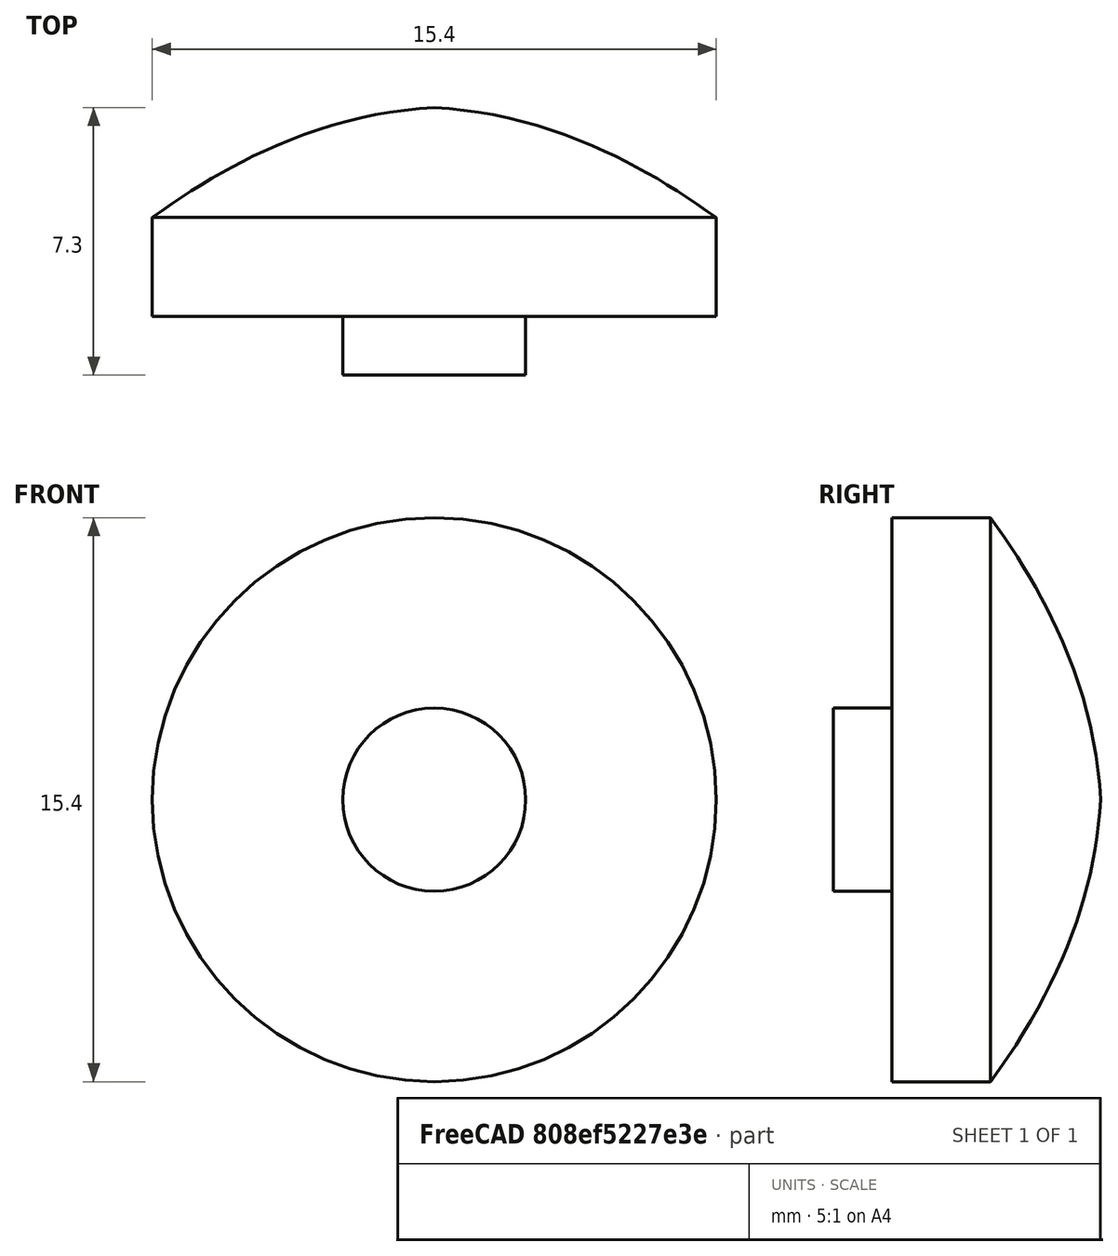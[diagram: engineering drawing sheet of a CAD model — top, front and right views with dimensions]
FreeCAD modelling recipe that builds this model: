
FCSTD DOCUMENT  (FreeCAD 0.19R0.19.2)
Label: headphoneStandNuthook
License: All rights reserved
LicenseURL: http://en.wikipedia.org/wiki/All_rights_reserved
objects: Sketcher::SketchObject×1, Part::Revolution×1
note: 2 computed .brp shape members not serialized (recipe doc carries the construction recipe); baked Part::Feature solids carry a one-line shape summary decoded from their .brp

FEATURE [Sketcher::SketchObject] Sketch
  FullyConstrained = true
  Placement = pos=(0,0,0) rot=(0.707107,0,0.707107;3.14159rad)
  sketch-geometry (11):
    g0: LineSegment StartX=-7.7 StartY=-1.5 StartZ=0 EndX=-2.5 EndY=-1.5 EndZ=0
    g1: LineSegment StartX=-2.5 StartY=0.1 StartZ=0 EndX=0 EndY=0.1 EndZ=0
    g2: LineSegment StartX=-7.7 StartY=-1.5 StartZ=0 EndX=-7.7 EndY=-4.2 EndZ=0
    g3: Circle CenterX=-7.7 CenterY=-4.2 CenterZ=0 NormalX=0 NormalY=0 NormalZ=1 AngleXU=0 Radius=1
    g4: Circle CenterX=-3.852 CenterY=-7.00779 CenterZ=0 NormalX=0 NormalY=0 NormalZ=1 AngleXU=0 Radius=1
    g5: Circle CenterX=0 CenterY=-7.2 CenterZ=0 NormalX=0 NormalY=0 NormalZ=1 AngleXU=0 Radius=1
    g6: BSplineCurve PolesCount=3 KnotsCount=2 Degree=2 IsPeriodic=0
    g7: GeomPoint X=-7.7 Y=-4.2 Z=0
    g8: GeomPoint X=0 Y=-7.2 Z=0
    g9: LineSegment StartX=-2.5 StartY=0.1 StartZ=0 EndX=-2.5 EndY=-1.5 EndZ=0
    g10: LineSegment StartX=0 StartY=0.1 StartZ=0 EndX=0 EndY=-7.2 EndZ=0
  constraints (24):
    c: Horizontal(g0)
    c: Distance(g0) = 5.2
    c: Horizontal(g1)
    c: Block(g0)
    c: Vertical(g2)
    c: Distance(g2) = 2.7
    c: Coincident(g2,g0)
    c: Weight(g3) = 1
    c: Equal(g3,g4)
    c: Equal(g3,g5)
    c: InternalAlignment(g3,g6)
    c: InternalAlignment(g4,g6)
    c: InternalAlignment(g5,g6)
    c: InternalAlignment(g7,g6)
    c: InternalAlignment(g8,g6)
    c: Coincident(g6,g2)
    c: Block(g6)
    c: Vertical(g9)
    c: Distance(g9) = 1.6
    c: Coincident(g9,g0)
    c: Vertical(g10)
    c: Coincident(g10,g6)
    c: Coincident(g1,g9)
    c: Coincident(g1,g10)
FEATURE [Part::Revolution] Revolve
  Angle = 360
  Axis = (0,1,0)
  Base = (0,0,0)
  FaceMakerClass = Part::FaceMakerBullseye
  Solid = true
  Source = -> Sketch
  Symmetric = false
